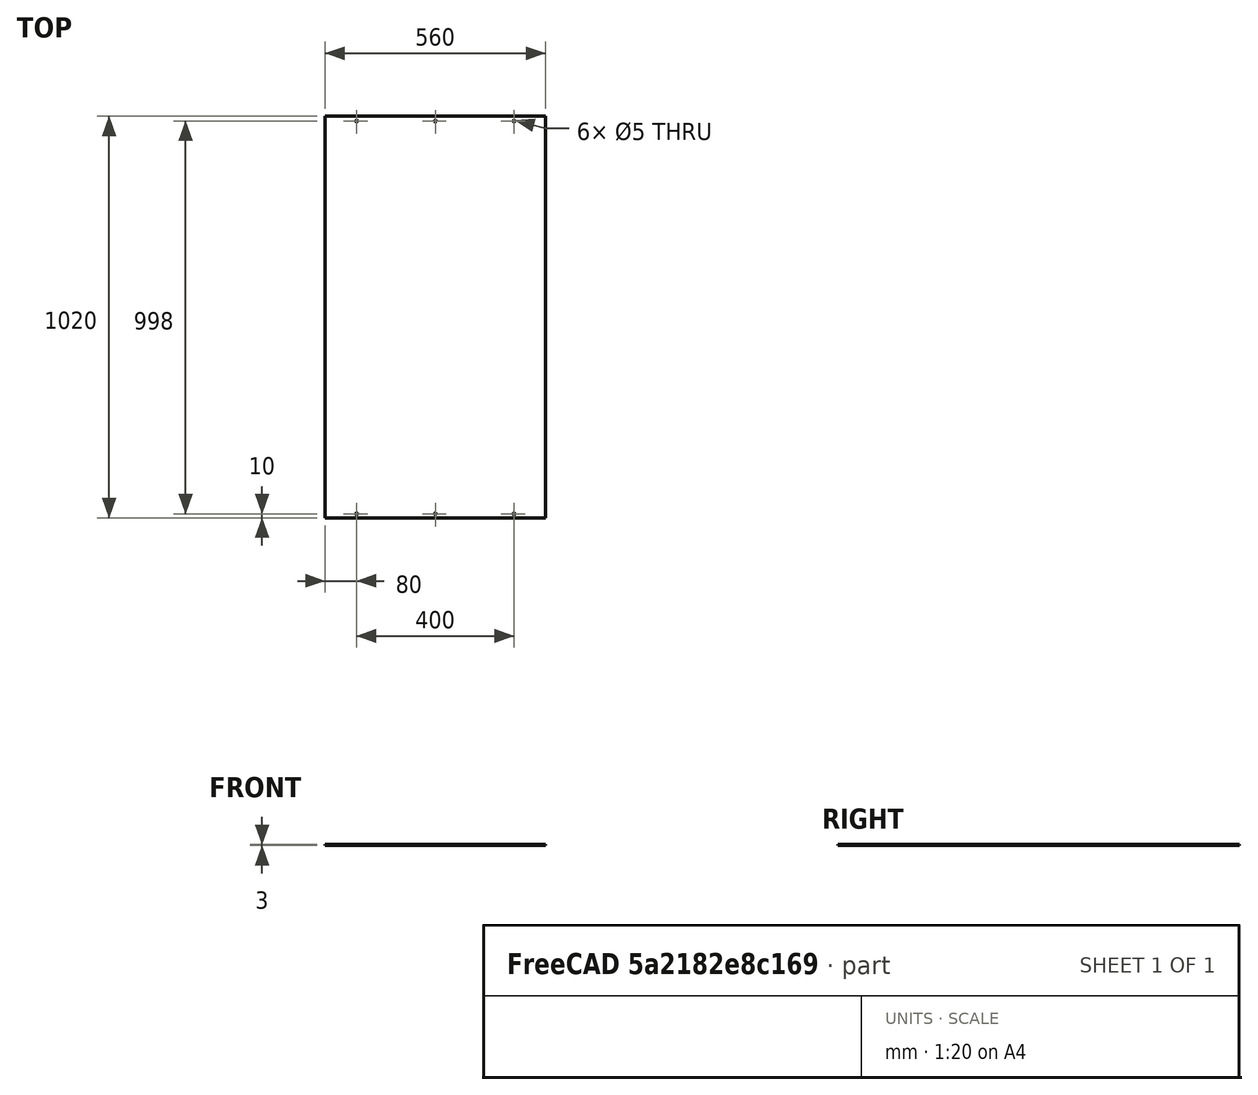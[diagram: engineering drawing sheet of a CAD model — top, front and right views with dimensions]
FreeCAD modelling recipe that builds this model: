
FCSTD DOCUMENT  (FreeCAD 0.16R6706 (Git))
Label: frame_cover
License: CreativeCommons Attribution-ShareAlike
LicenseURL: http://creativecommons.org/licenses/by-sa/4.0/
objects: Sketcher::SketchObject×1, PartDesign::Pad×1
note: 3 computed .brp shape members not serialized (recipe doc carries the construction recipe); baked Part::Feature solids carry a one-line shape summary decoded from their .brp

FEATURE [Sketcher::SketchObject] Sketch
  sketch-geometry (12):
    g0: LineSegment StartX=0 StartY=0 StartZ=0 EndX=560 EndY=0 EndZ=0
    g1: LineSegment StartX=560 StartY=0 StartZ=0 EndX=560 EndY=1020 EndZ=0
    g2: LineSegment StartX=560 StartY=1020 StartZ=0 EndX=0 EndY=1020 EndZ=0
    g3: LineSegment StartX=0 StartY=1020 StartZ=0 EndX=0 EndY=0 EndZ=0
    g4: Circle CenterX=80 CenterY=1008 CenterZ=0 NormalX=0 NormalY=0 NormalZ=1 Radius=2.5
    g5: Circle CenterX=280 CenterY=1008 CenterZ=0 NormalX=0 NormalY=0 NormalZ=1 Radius=2.5
    g6: Circle CenterX=480 CenterY=1008 CenterZ=0 NormalX=0 NormalY=0 NormalZ=1 Radius=2.5
    g7: LineSegment [constr] StartX=0 StartY=1008 StartZ=0 EndX=560 EndY=1008 EndZ=0
    g8: LineSegment [constr] StartX=0 StartY=10 StartZ=0 EndX=560 EndY=10 EndZ=0
    g9: Circle CenterX=80 CenterY=10 CenterZ=0 NormalX=0 NormalY=0 NormalZ=1 Radius=2.5
    g10: Circle CenterX=280 CenterY=10 CenterZ=0 NormalX=0 NormalY=0 NormalZ=1 Radius=2.5
    g11: Circle CenterX=480 CenterY=10 CenterZ=0 NormalX=0 NormalY=0 NormalZ=1 Radius=2.5
  constraints (37):
    c: Coincident(g0,g1)
    c: Coincident(g1,g2)
    c: Coincident(g2,g3)
    c: Coincident(g3,g0)
    c: Horizontal(g0)
    c: Horizontal(g2)
    c: Vertical(g1)
    c: Vertical(g3)
    c: Coincident(g0,g-1)
    c: DistanceY(g1,g1) = 1020
    c: DistanceX(g2,g2) = 560
    c: PointOnObject(g7,g3)
    c: Horizontal(g7)
    c: PointOnObject(g6,g7)
    c: PointOnObject(g5,g7)
    c: PointOnObject(g4,g7)
    c: DistanceY(g7,g1) = 12
    c: PointOnObject(g7,g1)
    c: DistanceX(g2,g4) = 80
    c: DistanceX(g6,g1) = 80
    c: DistanceX(g4,g5) = 200
    c: Equal(g4,g5)
    c: Equal(g5,g6)
    c: Radius(g6) = 2.5
    c: PointOnObject(g8,g3)
    c: PointOnObject(g8,g1)
    c: Horizontal(g8)
    c: DistanceY(g0,g8) = 10
    c: PointOnObject(g9,g8)
    c: PointOnObject(g10,g8)
    c: PointOnObject(g11,g8)
    c: DistanceX(g11,g0) = 80
    c: DistanceX(g-1,g9) = 80
    c: DistanceX(g9,g10) = 200
    c: Equal(g10,g9)
    c: Equal(g9,g11)
    c: Radius(g10) = 2.5
FEATURE [PartDesign::Pad] Pad
  Length = 3
  Length2 = 100
  Sketch = -> Sketch
  Type = 0
